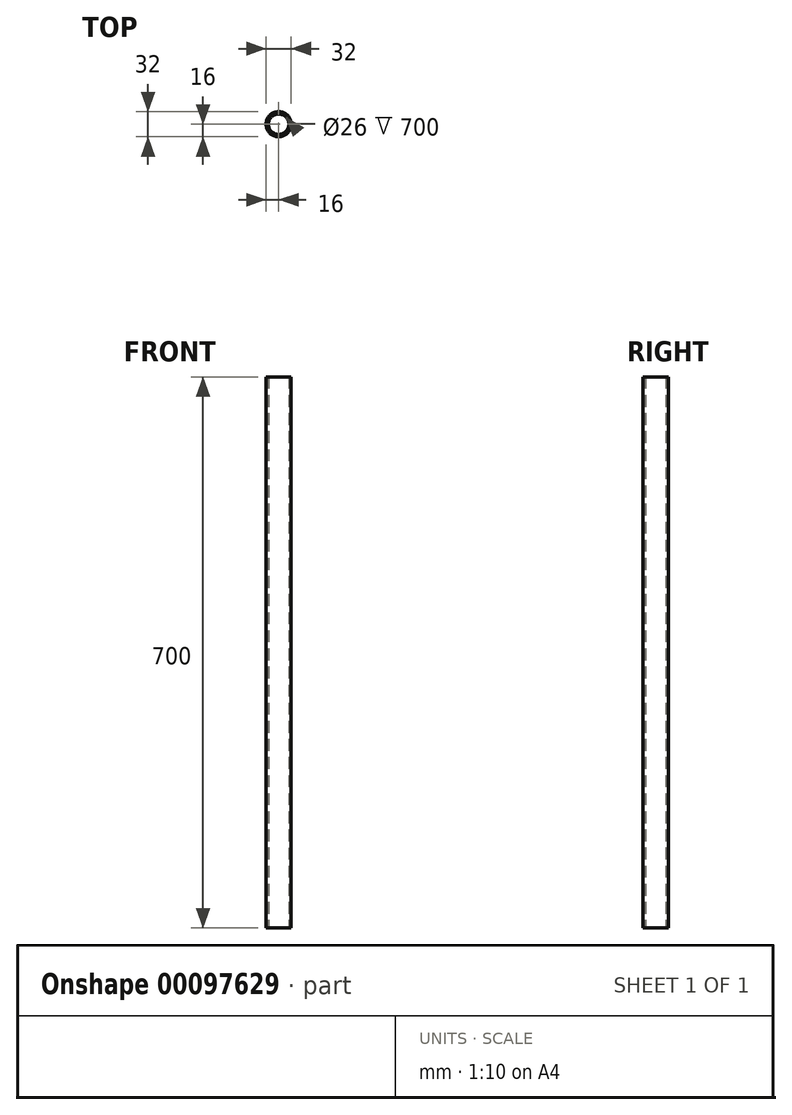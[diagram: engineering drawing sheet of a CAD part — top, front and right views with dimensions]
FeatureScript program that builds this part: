
annotation { "Feature Type Name" : "Feature", "Feature Type Description" : "" }
export const myFeature = defineFeature(function(context is Context, id is Id, definition is map)
    precondition{}
    {
        {
            var Q0;
            Q0=qCreatedBy(makeId("Top.planeOp"),FACE);
            var sketch = newSketch(context, id + "F0", { "sketchPlane" : qUnion([Q0])});
            skCircle(sketch, "E0", {"center": v(0, 0) * mm, "radius": 16 * mm});
            skCircle(sketch, "E1.0", {"center": v(0, 0) * mm, "radius": 13 * mm});
            skSolve(sketch);
        }
        {
            var Q0;
            Q0=makeQuery(id+"F0.imprint","IMPRINT",FACE,{"disambiguationData":[TD([[makeQuery(id+"F0.imprint","IMPRINT",EDGE,{"derivedFrom":sQuery(id+"F0.wireOp",EDGE,"E0")}),1.0]])]});
            extrude(context, id + "F1", {"entities" : qUnion([Q0]), "depth" : 700 * mm});
        }
    });
